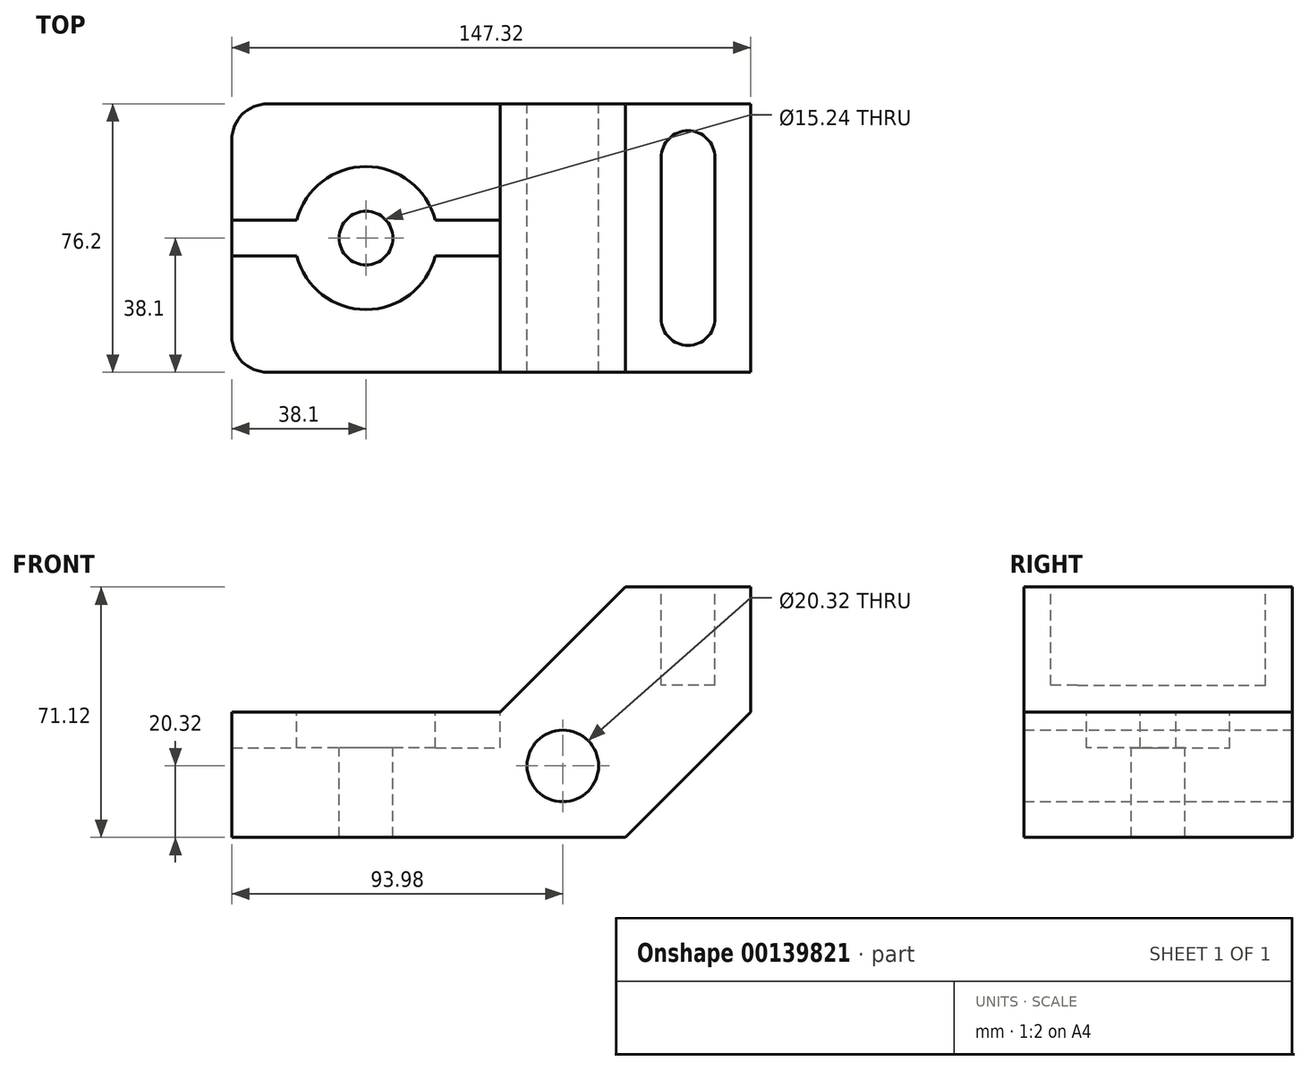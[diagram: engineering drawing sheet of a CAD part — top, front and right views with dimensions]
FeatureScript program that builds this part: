
annotation { "Feature Type Name" : "Feature", "Feature Type Description" : "" }
export const myFeature = defineFeature(function(context is Context, id is Id, definition is map)
    precondition{}
    {
        {
            var Q0;
            Q0=qCreatedBy(makeId("Front.planeOp"),FACE);
            var sketch = newSketch(context, id + "F0", { "sketchPlane" : qUnion([Q0])});
            skLineSegment(sketch, "E0", {"start": v(0, 0) * mm, "end": v(0, 35.56) * mm});
            skLineSegment(sketch, "E1", {"start": v(0, 35.56) * mm, "end": v(76.2, 35.56) * mm});
            skLineSegment(sketch, "E2", {"start": v(76.2, 35.56) * mm, "end": v(111.76, 71.12) * mm});
            skLineSegment(sketch, "E3", {"start": v(111.76, 71.12) * mm, "end": v(147.32, 71.12) * mm});
            skLineSegment(sketch, "E4", {"start": v(147.32, 71.12) * mm, "end": v(147.32, 35.56) * mm});
            skLineSegment(sketch, "E5", {"start": v(147.32, 35.56) * mm, "end": v(111.76, 0) * mm});
            skLineSegment(sketch, "E6", {"start": v(111.76, 0) * mm, "end": v(0, 0) * mm});
            skCircle(sketch, "E7", {"center": v(93.98, 20.32) * mm, "radius": 10.16 * mm});
            skSolve(sketch);
        }
        {
            var Q0;
            Q0 = qSketchRegion(id + "F0", true);
            extrude(context, id + "F1", {"entities" : qUnion([Q0]), "depth" : 76.2 * mm});
        }
        {
            var Q0;
            Q0=makeQuery(id+"F1.opExtrude","CAP_EDGE",EDGE,{"disambiguationData":[OSD([sQuery(id+"F0.wireOp",EDGE,"E0")])],"isStart":false});
            var Q1;
            Q1=makeQuery(id+"F1.opExtrude","CAP_EDGE",EDGE,{"disambiguationData":[OSD([sQuery(id+"F0.wireOp",EDGE,"E0")])],"isStart":true});
            fillet(context, id + "F2", {"entities" : qUnion([Q0, Q1]), "radius" : 10.16 * mm, "tangentPropagation" : true, "allowEdgeOverflow" : false});
        }
        {
            var Q0;
            Q0=makeQuery(id+"F1.opExtrude","SWEPT_FACE",FACE,{"disambiguationData":[OSD([sQuery(id+"F0.wireOp",EDGE,"E1")])]});
            var sketch = newSketch(context, id + "F3", { "sketchPlane" : qUnion([Q0])});
            skLineSegment(sketch, "E8.bottom", {"start": v(0, -33.02) * mm, "end": v(76.2, -33.02) * mm});
            skLineSegment(sketch, "E8.top", {"start": v(0, -43.18) * mm, "end": v(76.2, -43.18) * mm});
            skLineSegment(sketch, "E8.left", {"start": v(0, -33.02) * mm, "end": v(0, -43.18) * mm});
            skLineSegment(sketch, "E8.right", {"start": v(76.2, -33.02) * mm, "end": v(76.2, -43.18) * mm});
            skSolve(sketch);
        }
        {
            var Q0;
            Q0 = qSketchRegion(id + "F3", true);
            extrude(context, id + "F4", {"entities" : qUnion([Q0]), "operationType" : NewBodyOperationType.REMOVE, "oppositeDirection" : true, "depth" : 10.16 * mm});
        }
        {
            var Q0;
            Q0=makeQuery(id+"F1.opExtrude","SWEPT_FACE",FACE,{"disambiguationData":[OSD([sQuery(id+"F0.wireOp",EDGE,"E3")])]});
            var sketch = newSketch(context, id + "F5", { "sketchPlane" : qUnion([Q0])});
            skLineSegment(sketch, "E9", {"start": v(129.54, -15.24) * mm, "end": v(129.54, -60.96) * mm, "construction": true});
            skLineSegment(sketch, "E10", {"start": v(121.92, -15.24) * mm, "end": v(121.92, -60.96) * mm});
            skLineSegment(sketch, "E11", {"start": v(137.16, -60.96) * mm, "end": v(137.16, -15.24) * mm});
            skArc(sketch, "E12", {"start": v(137.16, -15.24) * mm, "mid": v(129.54, -7.62) * mm, "end": v(121.92, -15.24) * mm});
            skArc(sketch, "E13", {"start": v(121.92, -60.96) * mm, "mid": v(129.54, -68.58) * mm, "end": v(137.16, -60.96) * mm});
            skPoint(sketch, "E14", {"position": v(38.1, -38.1) * mm});
            skSolve(sketch);
        }
        {
            var Q0;
            Q0=makeQuery(id+"F5.imprint","IMPRINT",FACE,{"disambiguationData":[TD([[makeQuery(id+"F5.imprint","IMPRINT",EDGE,{"derivedFrom":sQuery(id+"F5.wireOp",EDGE,"E10")}),1.0]])]});
            extrude(context, id + "F6", {"entities" : qUnion([Q0]), "operationType" : NewBodyOperationType.REMOVE, "oppositeDirection" : true, "depth" : 27.94 * mm});
        }
        {
            var Q0;
            Q0=sQuery(id+"F5.wireOp",VERTEX,"E14");
            var Q1;
            Q1=makeQuery(id+"F1.opExtrude","SWEPT_BODY",BODY,{"disambiguationData":[OSD([sQuery(id+"F0.wireOp",EDGE,"E0"),sQuery(id+"F0.wireOp",EDGE,"E1"),sQuery(id+"F0.wireOp",EDGE,"E2"),sQuery(id+"F0.wireOp",EDGE,"E3"),sQuery(id+"F0.wireOp",EDGE,"E4"),sQuery(id+"F0.wireOp",EDGE,"E5"),sQuery(id+"F0.wireOp",EDGE,"E6"),sQuery(id+"F0.wireOp",EDGE,"E7")])]});
            hole(context, id + "F7", {"style" : HoleStyle.C_BORE, "endStyle" : HoleEndStyle.THROUGH, "holeDiameter" : 15.24 * mm, "cBoreDiameter" : 40.64 * mm, "cBoreDepth" : 0 * mm, "locations" : qUnion([Q0]), "scope" : qUnion([Q1]), "isTappedThrough" : true});
        }
    });
